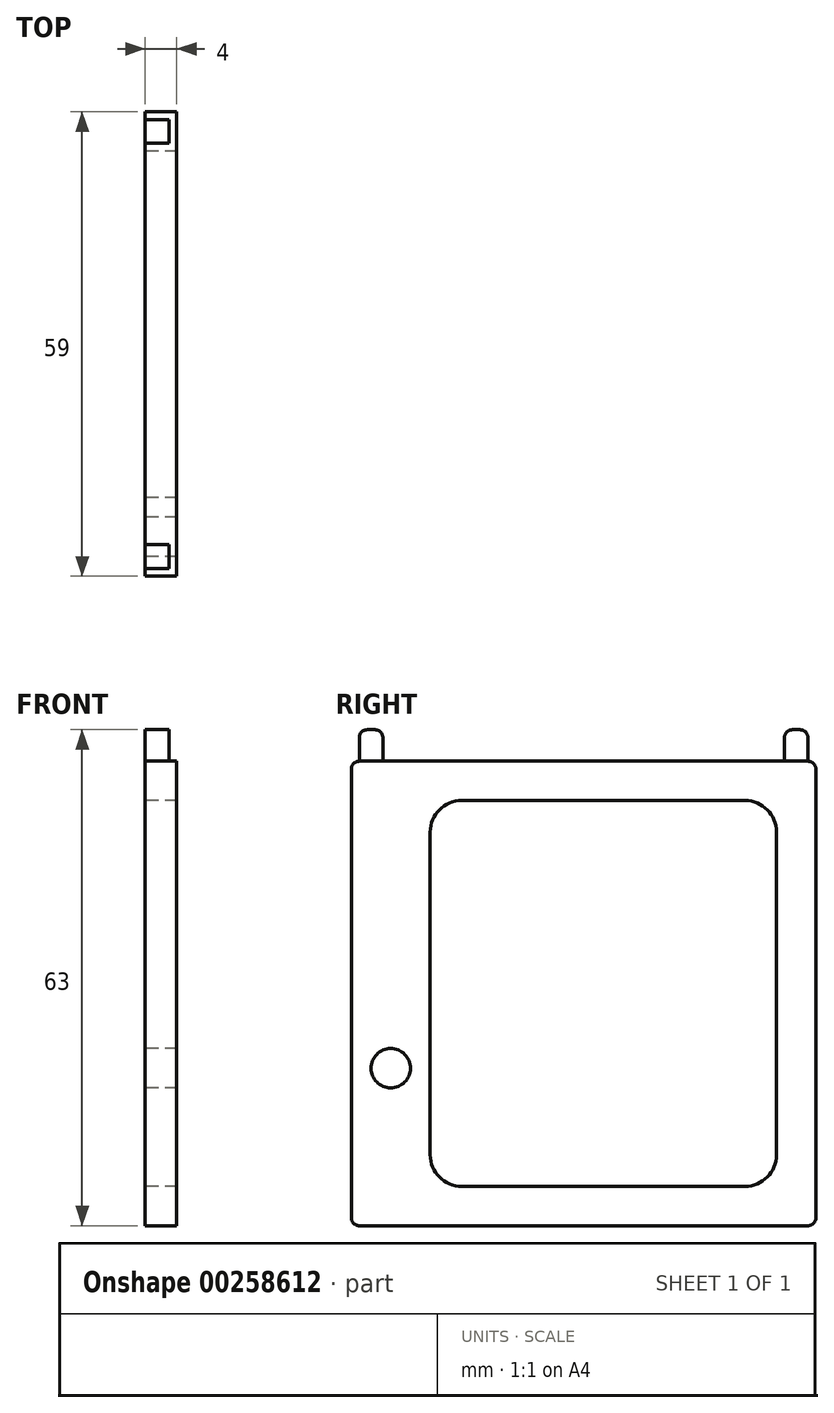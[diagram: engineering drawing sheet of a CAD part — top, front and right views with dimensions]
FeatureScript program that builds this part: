
annotation { "Feature Type Name" : "Feature", "Feature Type Description" : "" }
export const myFeature = defineFeature(function(context is Context, id is Id, definition is map)
    precondition{}
    {
        {
            var Q0;
            Q0=qCreatedBy(makeId("Right.planeOp"),FACE);
            var sketch = newSketch(context, id + "F0", { "sketchPlane" : qUnion([Q0])});
            skLineSegment(sketch, "E0.bottom", {"start": v(-29.5, 29.5) * mm, "end": v(29.5, 29.5) * mm});
            skLineSegment(sketch, "E0.top", {"start": v(-29.5, -29.5) * mm, "end": v(29.5, -29.5) * mm});
            skLineSegment(sketch, "E0.left", {"start": v(-29.5, 29.5) * mm, "end": v(-29.5, -29.5) * mm});
            skLineSegment(sketch, "E0.right", {"start": v(29.5, 29.5) * mm, "end": v(29.5, -29.5) * mm});
            skPoint(sketch, "E0.middle", {"position": v(0, 0) * mm});
            skLineSegment(sketch, "E1", {"start": v(-29.5, -29.5) * mm, "end": v(-28.5, -29.5) * mm, "construction": true});
            skLineSegment(sketch, "E2.bottom", {"start": v(-28.5, -29.5) * mm, "end": v(-25.5, -29.5) * mm});
            skLineSegment(sketch, "E2.top", {"start": v(-28.5, -33.5) * mm, "end": v(-25.5, -33.5) * mm});
            skLineSegment(sketch, "E2.left", {"start": v(-28.5, -29.5) * mm, "end": v(-28.5, -33.5) * mm});
            skLineSegment(sketch, "E2.right", {"start": v(-25.5, -29.5) * mm, "end": v(-25.5, -33.5) * mm});
            skLineSegment(sketch, "E3", {"start": v(29.5, -29.5) * mm, "end": v(28.5, -29.5) * mm, "construction": true});
            skLineSegment(sketch, "E4.bottom", {"start": v(28.5, -29.5) * mm, "end": v(25.5, -29.5) * mm});
            skLineSegment(sketch, "E4.top", {"start": v(28.5, -33.5) * mm, "end": v(25.5, -33.5) * mm});
            skLineSegment(sketch, "E4.left", {"start": v(28.5, -29.5) * mm, "end": v(28.5, -33.5) * mm});
            skLineSegment(sketch, "E4.right", {"start": v(25.5, -29.5) * mm, "end": v(25.5, -33.5) * mm});
            skLineSegment(sketch, "E5.1.0", {"start": v(-28.5, 33.5) * mm, "end": v(-25.5, 33.5) * mm});
            skLineSegment(sketch, "E5.1.1", {"start": v(-29.5, 29.5) * mm, "end": v(-28.5, 29.5) * mm, "construction": true});
            skLineSegment(sketch, "E5.1.2", {"start": v(-28.5, 29.5) * mm, "end": v(-28.5, 33.5) * mm});
            skLineSegment(sketch, "E5.1.3", {"start": v(-28.5, 29.5) * mm, "end": v(-25.5, 29.5) * mm});
            skLineSegment(sketch, "E5.1.4", {"start": v(-25.5, 29.5) * mm, "end": v(-25.5, 33.5) * mm});
            skLineSegment(sketch, "E5.anchor1", {"start": v(0, 0) * mm, "end": v(25.5, -33.5) * mm, "construction": true});
            skLineSegment(sketch, "E5.anchor2", {"start": v(0, 0) * mm, "end": v(-25.5, 33.5) * mm, "construction": true});
            skLineSegment(sketch, "E6.1.0", {"start": v(28.5, 33.5) * mm, "end": v(25.5, 33.5) * mm});
            skLineSegment(sketch, "E6.1.1", {"start": v(28.5, 29.5) * mm, "end": v(25.5, 29.5) * mm});
            skLineSegment(sketch, "E6.1.2", {"start": v(29.5, 29.5) * mm, "end": v(28.5, 29.5) * mm, "construction": true});
            skLineSegment(sketch, "E6.1.3", {"start": v(28.5, 29.5) * mm, "end": v(28.5, 33.5) * mm});
            skLineSegment(sketch, "E6.1.4", {"start": v(25.5, 29.5) * mm, "end": v(25.5, 33.5) * mm});
            skLineSegment(sketch, "E7.bottom", {"start": v(-29.5, -29.5) * mm, "end": v(-24.5, -29.5) * mm, "construction": true});
            skLineSegment(sketch, "E7.top", {"start": v(-29.5, -9.5) * mm, "end": v(-24.5, -9.5) * mm, "construction": true});
            skLineSegment(sketch, "E7.left", {"start": v(-29.5, -29.5) * mm, "end": v(-29.5, -9.5) * mm, "construction": true});
            skLineSegment(sketch, "E7.right", {"start": v(-24.5, -29.5) * mm, "end": v(-24.5, -9.5) * mm, "construction": true});
            skCircle(sketch, "E8", {"center": v(-24.5, -9.5) * mm, "radius": 2.5 * mm});
            skLineSegment(sketch, "E9.bottom", {"start": v(-19.5, -24.5) * mm, "end": v(19.5, -24.5) * mm});
            skLineSegment(sketch, "E9.top", {"start": v(-19.5, 24.5) * mm, "end": v(19.5, 24.5) * mm});
            skLineSegment(sketch, "E9.left", {"start": v(-19.5, -24.5) * mm, "end": v(-19.5, 24.5) * mm});
            skLineSegment(sketch, "E9.right", {"start": v(19.5, -24.5) * mm, "end": v(19.5, 24.5) * mm});
            skLineSegment(sketch, "E10.bottom", {"start": v(19.5, 24.5) * mm, "end": v(24.5, 24.5) * mm});
            skLineSegment(sketch, "E10.top", {"start": v(19.5, -24.5) * mm, "end": v(24.5, -24.5) * mm});
            skLineSegment(sketch, "E10.left", {"start": v(19.5, 24.5) * mm, "end": v(19.5, -24.5) * mm});
            skLineSegment(sketch, "E10.right", {"start": v(24.5, 24.5) * mm, "end": v(24.5, -24.5) * mm});
            skSolve(sketch);
        }
        {
            var Q0;
            {var subQ1=sQuery(id+"F0.wireOp",EDGE,"E0.left");Q0=makeQuery(id+"F0.imprint","IMPRINT",FACE,{"disambiguationData":[TD([[makeQuery(id+"F0.imprint","IMPRINT",EDGE,{"derivedFrom":subQ1}),1.0]])]});}
            var Q1;
            Q1=makeQuery(id+"F0.imprint","IMPRINT",FACE,{"disambiguationData":[TD([[makeQuery(id+"F0.imprint","IMPRINT",EDGE,{"derivedFrom":sQuery(id+"F0.wireOp",EDGE,"E5.1.0")}),-1.0]])]});
            var Q2;
            Q2=makeQuery(id+"F0.imprint","IMPRINT",FACE,{"disambiguationData":[TD([[makeQuery(id+"F0.imprint","IMPRINT",EDGE,{"derivedFrom":sQuery(id+"F0.wireOp",EDGE,"E6.1.0")}),1.0]])]});
            var Q3;
            Q3=makeQuery(id+"F0.imprint","IMPRINT",FACE,{"disambiguationData":[TD([[makeQuery(id+"F0.imprint","IMPRINT",EDGE,{"derivedFrom":sQuery(id+"F0.wireOp",EDGE,"E2.bottom")}),-1.0]])]});
            var Q4;
            Q4=makeQuery(id+"F0.imprint","IMPRINT",FACE,{"disambiguationData":[TD([[makeQuery(id+"F0.imprint","IMPRINT",EDGE,{"derivedFrom":sQuery(id+"F0.wireOp",EDGE,"E4.bottom")}),1.0]])]});
            extrude(context, id + "F1", {"entities" : qUnion([Q0, Q1, Q2, Q3, Q4]), "depth" : 4 * mm});
        }
        {
            var Q0;
            Q0=makeQuery(id+"F1.opExtrude","CAP_FACE",FACE,{"disambiguationData":[OSD([sQuery(id+"F0.wireOp",EDGE,"E0.bottom"),sQuery(id+"F0.wireOp",EDGE,"E0.top"),sQuery(id+"F0.wireOp",EDGE,"E0.left"),sQuery(id+"F0.wireOp",EDGE,"E0.right"),sQuery(id+"F0.wireOp",EDGE,"E2.top"),sQuery(id+"F0.wireOp",EDGE,"E2.left"),sQuery(id+"F0.wireOp",EDGE,"E2.right"),sQuery(id+"F0.wireOp",EDGE,"E4.top"),sQuery(id+"F0.wireOp",EDGE,"E4.left"),sQuery(id+"F0.wireOp",EDGE,"E4.right"),sQuery(id+"F0.wireOp",EDGE,"E5.1.0"),sQuery(id+"F0.wireOp",EDGE,"E5.1.2"),sQuery(id+"F0.wireOp",EDGE,"E5.1.4"),sQuery(id+"F0.wireOp",EDGE,"E6.1.0"),sQuery(id+"F0.wireOp",EDGE,"E6.1.3"),sQuery(id+"F0.wireOp",EDGE,"E6.1.4"),sQuery(id+"F0.wireOp",EDGE,"E8"),sQuery(id+"F0.wireOp",EDGE,"E9.bottom"),sQuery(id+"F0.wireOp",EDGE,"E9.top"),sQuery(id+"F0.wireOp",EDGE,"E9.left"),sQuery(id+"F0.wireOp",EDGE,"E10.bottom"),sQuery(id+"F0.wireOp",EDGE,"E10.top"),sQuery(id+"F0.wireOp",EDGE,"E10.right")])],"isStart":false});
            var sketch = newSketch(context, id + "F2", { "sketchPlane" : qUnion([Q0])});
            skLineSegment(sketch, "E11.bottom", {"start": v(-28.5, 33.5) * mm, "end": v(-25.5, 33.5) * mm});
            skLineSegment(sketch, "E11.top", {"start": v(-28.5, 29.5) * mm, "end": v(-25.5, 29.5) * mm});
            skLineSegment(sketch, "E11.left", {"start": v(-28.5, 33.5) * mm, "end": v(-28.5, 29.5) * mm});
            skLineSegment(sketch, "E11.right", {"start": v(-25.5, 33.5) * mm, "end": v(-25.5, 29.5) * mm});
            skLineSegment(sketch, "E12.bottom", {"start": v(25.5, 33.5) * mm, "end": v(28.5, 33.5) * mm});
            skLineSegment(sketch, "E12.top", {"start": v(25.5, 29.5) * mm, "end": v(28.5, 29.5) * mm});
            skLineSegment(sketch, "E12.left", {"start": v(25.5, 33.5) * mm, "end": v(25.5, 29.5) * mm});
            skLineSegment(sketch, "E12.right", {"start": v(28.5, 33.5) * mm, "end": v(28.5, 29.5) * mm});
            skLineSegment(sketch, "E13.bottom", {"start": v(-28.5, -33.5) * mm, "end": v(-25.5, -33.5) * mm});
            skLineSegment(sketch, "E13.top", {"start": v(-28.5, -29.5) * mm, "end": v(-25.5, -29.5) * mm});
            skLineSegment(sketch, "E13.left", {"start": v(-28.5, -33.5) * mm, "end": v(-28.5, -29.5) * mm});
            skLineSegment(sketch, "E13.right", {"start": v(-25.5, -33.5) * mm, "end": v(-25.5, -29.5) * mm});
            skLineSegment(sketch, "E14.bottom", {"start": v(25.5, -33.5) * mm, "end": v(28.5, -33.5) * mm});
            skLineSegment(sketch, "E14.top", {"start": v(25.5, -29.5) * mm, "end": v(28.5, -29.5) * mm});
            skLineSegment(sketch, "E14.left", {"start": v(25.5, -33.5) * mm, "end": v(25.5, -29.5) * mm});
            skLineSegment(sketch, "E14.right", {"start": v(28.5, -33.5) * mm, "end": v(28.5, -29.5) * mm});
            skSolve(sketch);
        }
        {
            var Q0;
            Q0 = qSketchRegion(id + "F2", true);
            extrude(context, id + "F3", {"entities" : qUnion([Q0]), "operationType" : NewBodyOperationType.REMOVE, "oppositeDirection" : true, "depth" : 1 * mm});
        }
        {
            var Q0;
            Q0=makeQuery(id+"F1.opExtrude","SWEPT_EDGE",EDGE,{"disambiguationData":[OSD([sQuery(id+"F0.wireOp",EDGE,"E9.top"),sQuery(id+"F0.wireOp",EDGE,"E9.left")])]});
            var Q1;
            Q1=makeQuery(id+"F1.opExtrude","SWEPT_EDGE",EDGE,{"disambiguationData":[OSD([sQuery(id+"F0.wireOp",EDGE,"E10.bottom"),sQuery(id+"F0.wireOp",EDGE,"E10.right")])]});
            var Q2;
            Q2=makeQuery(id+"F1.opExtrude","SWEPT_EDGE",EDGE,{"disambiguationData":[OSD([sQuery(id+"F0.wireOp",EDGE,"E10.top"),sQuery(id+"F0.wireOp",EDGE,"E10.right")])]});
            var Q3;
            Q3=makeQuery(id+"F1.opExtrude","SWEPT_EDGE",EDGE,{"disambiguationData":[OSD([sQuery(id+"F0.wireOp",EDGE,"E9.bottom"),sQuery(id+"F0.wireOp",EDGE,"E9.left")])]});
            fillet(context, id + "F4", {"entities" : qUnion([Q0, Q1, Q2, Q3]), "radius" : 4 * mm, "tangentPropagation" : true, "allowEdgeOverflow" : false});
        }
        {
            var Q0;
            Q0=makeQuery(id+"F1.opExtrude","SWEPT_EDGE",EDGE,{"disambiguationData":[OSD([sQuery(id+"F0.wireOp",EDGE,"E5.1.0"),sQuery(id+"F0.wireOp",EDGE,"E5.1.2")])]});
            var Q1;
            Q1=makeQuery(id+"F1.opExtrude","SWEPT_EDGE",EDGE,{"disambiguationData":[OSD([sQuery(id+"F0.wireOp",EDGE,"E0.bottom"),sQuery(id+"F0.wireOp",EDGE,"E0.left")])]});
            var Q2;
            Q2=makeQuery(id+"F1.opExtrude","SWEPT_EDGE",EDGE,{"disambiguationData":[OSD([sQuery(id+"F0.wireOp",EDGE,"E5.1.0"),sQuery(id+"F0.wireOp",EDGE,"E5.1.4")])]});
            var Q3;
            Q3=makeQuery(id+"F1.opExtrude","SWEPT_EDGE",EDGE,{"disambiguationData":[OSD([sQuery(id+"F0.wireOp",EDGE,"E6.1.0"),sQuery(id+"F0.wireOp",EDGE,"E6.1.4")])]});
            var Q4;
            Q4=makeQuery(id+"F1.opExtrude","SWEPT_EDGE",EDGE,{"disambiguationData":[OSD([sQuery(id+"F0.wireOp",EDGE,"E6.1.0"),sQuery(id+"F0.wireOp",EDGE,"E6.1.3")])]});
            var Q5;
            Q5=makeQuery(id+"F1.opExtrude","SWEPT_EDGE",EDGE,{"disambiguationData":[OSD([sQuery(id+"F0.wireOp",EDGE,"E0.bottom"),sQuery(id+"F0.wireOp",EDGE,"E0.right")])]});
            var Q6;
            Q6=makeQuery(id+"F1.opExtrude","SWEPT_EDGE",EDGE,{"disambiguationData":[OSD([sQuery(id+"F0.wireOp",EDGE,"E2.top"),sQuery(id+"F0.wireOp",EDGE,"E2.right")])]});
            var Q7;
            Q7=makeQuery(id+"F1.opExtrude","SWEPT_EDGE",EDGE,{"disambiguationData":[OSD([sQuery(id+"F0.wireOp",EDGE,"E2.top"),sQuery(id+"F0.wireOp",EDGE,"E2.left")])]});
            var Q8;
            Q8=makeQuery(id+"F1.opExtrude","SWEPT_EDGE",EDGE,{"disambiguationData":[OSD([sQuery(id+"F0.wireOp",EDGE,"E0.top"),sQuery(id+"F0.wireOp",EDGE,"E0.left")])]});
            var Q9;
            Q9=makeQuery(id+"F1.opExtrude","SWEPT_EDGE",EDGE,{"disambiguationData":[OSD([sQuery(id+"F0.wireOp",EDGE,"E4.top"),sQuery(id+"F0.wireOp",EDGE,"E4.right")])]});
            var Q10;
            Q10=makeQuery(id+"F1.opExtrude","SWEPT_EDGE",EDGE,{"disambiguationData":[OSD([sQuery(id+"F0.wireOp",EDGE,"E4.top"),sQuery(id+"F0.wireOp",EDGE,"E4.left")])]});
            var Q11;
            Q11=makeQuery(id+"F1.opExtrude","SWEPT_EDGE",EDGE,{"disambiguationData":[OSD([sQuery(id+"F0.wireOp",EDGE,"E0.top"),sQuery(id+"F0.wireOp",EDGE,"E0.right")])]});
            fillet(context, id + "F5", {"entities" : qUnion([Q0, Q1, Q2, Q3, Q4, Q5, Q6, Q7, Q8, Q9, Q10, Q11]), "radius" : 1 * mm, "tangentPropagation" : true, "allowEdgeOverflow" : false});
        }
    });
